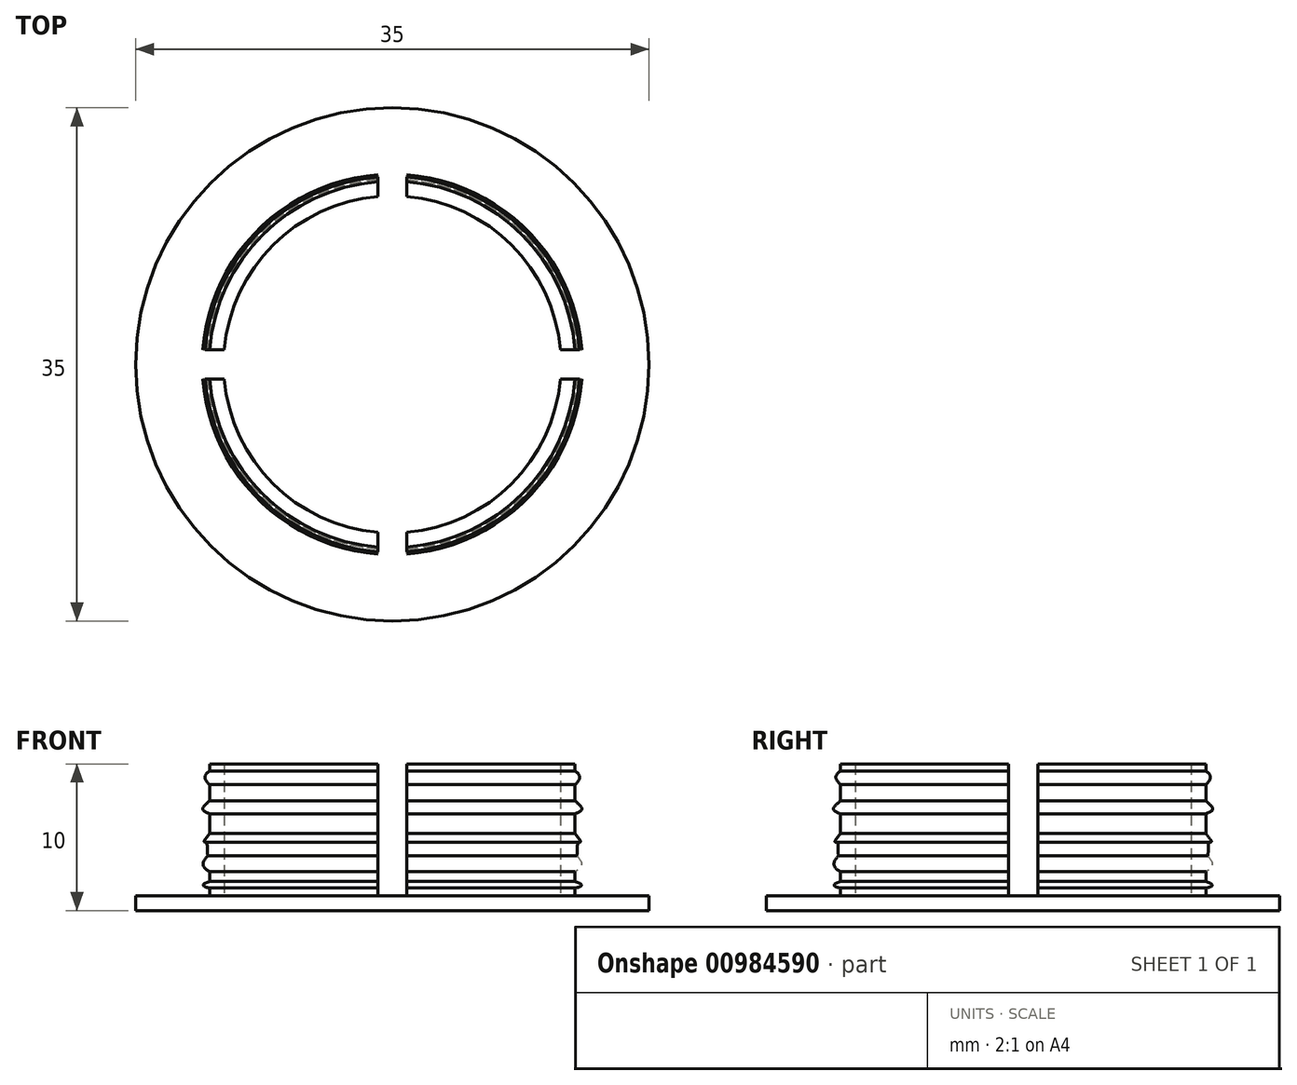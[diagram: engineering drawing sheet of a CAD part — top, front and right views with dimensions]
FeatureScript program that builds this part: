
annotation { "Feature Type Name" : "Feature", "Feature Type Description" : "" }
export const myFeature = defineFeature(function(context is Context, id is Id, definition is map)
    precondition{}
    {
        {
            var Q0;
            Q0=qCreatedBy(makeId("Top.planeOp"),FACE);
            var sketch = newSketch(context, id + "F0", { "sketchPlane" : qUnion([Q0])});
            skCircle(sketch, "E0", {"center": v(0, 0) * mm, "radius": 17.5 * mm});
            skCircle(sketch, "E1", {"center": v(0, 0) * mm, "radius": 12.5 * mm});
            skSolve(sketch);
        }
        {
            var Q0;
            Q0=makeQuery(id+"F0.imprint","IMPRINT",FACE,{"disambiguationData":[TD([[makeQuery(id+"F0.imprint","IMPRINT",EDGE,{"derivedFrom":sQuery(id+"F0.wireOp",EDGE,"E0")}),1.0]])]});
            var Q1;
            Q1=makeQuery(id+"F0.imprint","IMPRINT",FACE,{"disambiguationData":[TD([[makeQuery(id+"F0.imprint","IMPRINT",EDGE,{"derivedFrom":sQuery(id+"F0.wireOp",EDGE,"E1")}),1.0]])]});
            extrude(context, id + "F1", {"entities" : qUnion([Q0, Q1]), "depth" : 1 * mm, "offsetDistance" : 25 * mm});
        }
        {
            var Q0;
            Q0=makeQuery(id+"F0.imprint","IMPRINT",FACE,{"disambiguationData":[TD([[makeQuery(id+"F0.imprint","IMPRINT",EDGE,{"derivedFrom":sQuery(id+"F0.wireOp",EDGE,"E1")}),1.0]])]});
            extrude(context, id + "F2", {"entities" : qUnion([Q0]), "operationType" : NewBodyOperationType.ADD, "depth" : 10 * mm, "offsetDistance" : 25 * mm});
        }
        {
            var Q0;
            Q0=qCreatedBy(makeId("Right.planeOp"),FACE);
            var sketch = newSketch(context, id + "F3", { "sketchPlane" : qUnion([Q0])});
            skFitSpline(sketch, "E2", {"points": [v(-12.46, 3.44) * mm, v(-12.71, 4.65) * mm, v(-12.88, 4.7) * mm, v(-12.08, 6.2) * mm, v(-12.96, 6.92) * mm, v(-12.12, 8) * mm, v(-12.8, 9.01) * mm, v(-11.96, 9.56) * mm, v(-9.4, 4.65) * mm, v(-12.46, 3.44) * mm]});
            skFitSpline(sketch, "E3", {"points": [v(-11.45, 1.8) * mm, v(-12.92, 1.76) * mm, v(-11.87, 2.3) * mm, v(-12.92, 3.06) * mm, v(-11.37, 4.23) * mm, v(-11.45, 1.8) * mm]});
            skSolve(sketch);
        }
        {
            var Q0;
            Q0 = qSketchRegion(id + "F3", true);
            var Q1;
            Q1=makeQuery(id+"F2.opExtrude","SWEPT_FACE",FACE,{"disambiguationData":[OSD([sQuery(id+"F0.wireOp",EDGE,"E1")])]});
            revolve(context, id + "F4", {"operationType" : NewBodyOperationType.ADD, "surfaceOperationType" : NewSurfaceOperationType.NEW, "entities" : qUnion([Q0]), "axis" : qUnion([Q1]), "revolveType" : RevolveType.FULL});
        }
        {
            var Q0;
            Q0=makeQuery(id+"F2.opExtrude","CAP_FACE",FACE,{"disambiguationData":[OSD([sQuery(id+"F0.wireOp",EDGE,"E1")])],"isStart":false});
            shell(context, id + "F5", {"entities" : qUnion([Q0]), "thickness" : 1 * mm});
        }
        {
            var Q0;
            Q0=qCreatedBy(makeId("Top.planeOp"),FACE);
            var sketch = newSketch(context, id + "F6", { "sketchPlane" : qUnion([Q0])});
            skLineSegment(sketch, "E4", {"start": v(0, 0) * mm, "end": v(0, -30) * mm, "construction": true});
            skLineSegment(sketch, "E5", {"start": v(0, -30) * mm, "end": v(-1, -30) * mm, "construction": true});
            skLineSegment(sketch, "E6.bottom", {"start": v(-1, -30) * mm, "end": v(1, -30) * mm});
            skLineSegment(sketch, "E6.top", {"start": v(-1, 26.37) * mm, "end": v(1, 26.37) * mm});
            skLineSegment(sketch, "E6.left", {"start": v(-1, -30) * mm, "end": v(-1, 26.37) * mm});
            skLineSegment(sketch, "E6.right", {"start": v(1, -30) * mm, "end": v(1, 26.37) * mm});
            skLineSegment(sketch, "E7.1.0", {"start": v(-21.92, -20.5) * mm, "end": v(-20.5, -21.92) * mm});
            skLineSegment(sketch, "E7.1.1", {"start": v(17.94, 19.35) * mm, "end": v(19.35, 17.94) * mm});
            skLineSegment(sketch, "E7.1.2", {"start": v(-21.92, -20.5) * mm, "end": v(17.94, 19.35) * mm});
            skLineSegment(sketch, "E7.1.3", {"start": v(-20.5, -21.92) * mm, "end": v(19.35, 17.94) * mm});
            skLineSegment(sketch, "E7.2.0", {"start": v(-30, 1) * mm, "end": v(-30, -1) * mm});
            skLineSegment(sketch, "E7.2.1", {"start": v(26.37, 1) * mm, "end": v(26.37, -1) * mm});
            skLineSegment(sketch, "E7.2.2", {"start": v(-30, 1) * mm, "end": v(26.37, 1) * mm});
            skLineSegment(sketch, "E7.2.3", {"start": v(-30, -1) * mm, "end": v(26.37, -1) * mm});
            skPoint(sketch, "E7.center", {"position": v(0, 0) * mm});
            skLineSegment(sketch, "E7.anchor1", {"start": v(0, 0) * mm, "end": v(-1, -30) * mm, "construction": true});
            skLineSegment(sketch, "E7.anchor2", {"start": v(0, 0) * mm, "end": v(-30, 1) * mm, "construction": true});
            skSolve(sketch);
        }
        {
            var Q0;
            {var subQ1=sQuery(id+"F6.wireOp",EDGE,"E7.2.1");Q0=makeQuery(id+"F6.imprint","IMPRINT",FACE,{"disambiguationData":[TD([[makeQuery(id+"F6.imprint","IMPRINT",EDGE,{"derivedFrom":subQ1}),-1.0]])]});}
            var Q1;
            {var subQ1=sQuery(id+"F6.wireOp",EDGE,"E7.2.0");Q1=makeQuery(id+"F6.imprint","IMPRINT",FACE,{"disambiguationData":[TD([[makeQuery(id+"F6.imprint","IMPRINT",EDGE,{"derivedFrom":subQ1}),1.0]])]});}
            var Q2;
            {var subQ1=sQuery(id+"F6.wireOp",EDGE,"E6.bottom");Q2=makeQuery(id+"F6.imprint","IMPRINT",FACE,{"disambiguationData":[TD([[makeQuery(id+"F6.imprint","IMPRINT",EDGE,{"derivedFrom":subQ1}),1.0]])]});}
            var Q3;
            {var subQ6=sQuery(id+"F6.wireOp",EDGE,"E6.top");Q3=makeQuery(id+"F6.imprint","IMPRINT",FACE,{"disambiguationData":[TD([[makeQuery(id+"F6.imprint","IMPRINT",EDGE,{"derivedFrom":subQ6}),-1.0]])]});}
            extrude(context, id + "F7", {"entities" : qUnion([Q0, Q1, Q2, Q3]), "operationType" : NewBodyOperationType.REMOVE, "depth" : 25 * mm, "offsetDistance" : 25 * mm});
        }
        {
            var Q0;
            Q0=makeQuery(id+"F0.imprint","IMPRINT",FACE,{"disambiguationData":[TD([[makeQuery(id+"F0.imprint","IMPRINT",EDGE,{"derivedFrom":sQuery(id+"F0.wireOp",EDGE,"E0")}),1.0]])]});
            var Q1;
            Q1=makeQuery(id+"F0.imprint","IMPRINT",FACE,{"disambiguationData":[TD([[makeQuery(id+"F0.imprint","IMPRINT",EDGE,{"derivedFrom":sQuery(id+"F0.wireOp",EDGE,"E1")}),1.0]])]});
            extrude(context, id + "F8", {"entities" : qUnion([Q0, Q1]), "operationType" : NewBodyOperationType.ADD, "depth" : 1 * mm, "offsetDistance" : 25 * mm});
        }
    });
